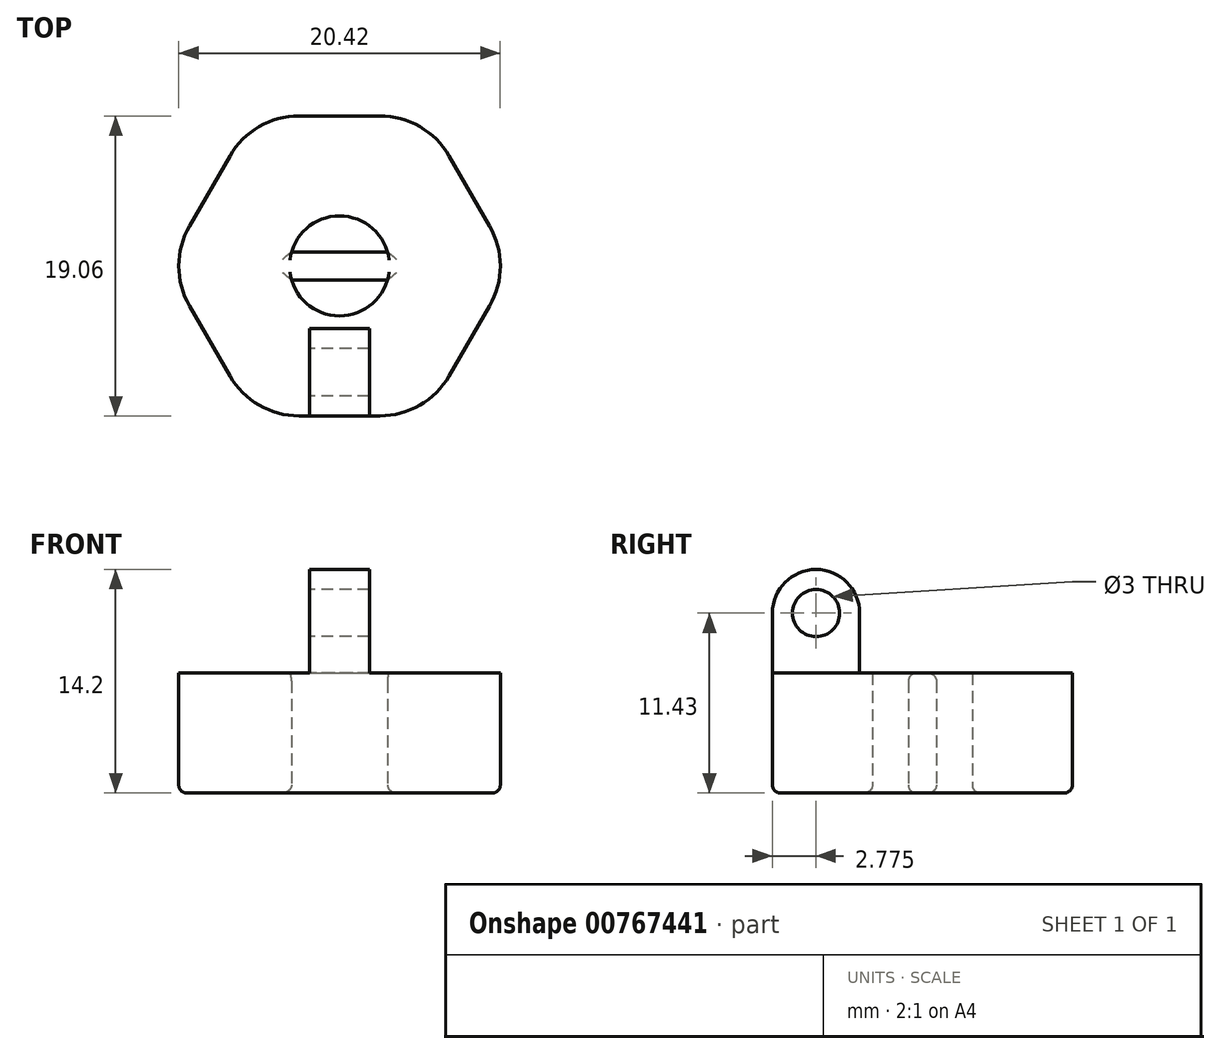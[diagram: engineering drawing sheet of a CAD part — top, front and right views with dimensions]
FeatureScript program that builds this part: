
annotation { "Feature Type Name" : "Feature", "Feature Type Description" : "" }
export const myFeature = defineFeature(function(context is Context, id is Id, definition is map)
    precondition{}
    {
        {
            var Q0;
            Q0=qCreatedBy(makeId("Top.planeOp"),FACE);
            var sketch = newSketch(context, id + "F0", { "sketchPlane" : qUnion([Q0])});
            skCircle(sketch, "E0.cCircle", {"center": v(0, 0) * mm, "radius": 9.53 * mm, "construction": true});
            skLineSegment(sketch, "E0.0", {"start": v(5.5, 9.53) * mm, "end": v(11, 0) * mm});
            skLineSegment(sketch, "E0.1", {"start": v(11, 0) * mm, "end": v(5.5, -9.53) * mm});
            skLineSegment(sketch, "E0.2", {"start": v(5.5, -9.53) * mm, "end": v(-5.5, -9.53) * mm});
            skLineSegment(sketch, "E0.3", {"start": v(-5.5, -9.53) * mm, "end": v(-11, 0) * mm});
            skLineSegment(sketch, "E0.4", {"start": v(-11, 0) * mm, "end": v(-5.5, 9.52) * mm});
            skLineSegment(sketch, "E0.5", {"start": v(-5.5, 9.52) * mm, "end": v(5.5, 9.52) * mm});
            skPoint(sketch, "E0.0.midPoint", {"position": v(8.25, 4.76) * mm});
            skCircle(sketch, "E1", {"center": v(0, 0) * mm, "radius": 3.18 * mm});
            skLineSegment(sketch, "E2.bottom", {"start": v(3.05, -0.89) * mm, "end": v(3.05, 0.89) * mm});
            skLineSegment(sketch, "E2.top", {"start": v(-3.05, -0.89) * mm, "end": v(-3.05, 0.89) * mm});
            skLineSegment(sketch, "E2.left", {"start": v(3.05, -0.89) * mm, "end": v(-3.05, -0.89) * mm});
            skLineSegment(sketch, "E2.right", {"start": v(3.05, 0.89) * mm, "end": v(-3.05, 0.89) * mm});
            skSolve(sketch);
        }
        {
            var Q0;
            Q0 = qSketchRegion(id + "F0", true);
            var Q1;
            Q1=makeQuery(id+"F0.imprint","IMPRINT",FACE,{"disambiguationData":[TD([[makeQuery(id+"F0.imprint","IMPRINT",EDGE,{"derivedFrom":sQuery(id+"F0.wireOp",EDGE,"E2.bottom")}),1.0]])]});
            var Q2;
            {var subQ0=sQuery(id+"F0.wireOp",EDGE,"E2.top");Q2=makeQuery(id+"F0.imprint","IMPRINT",FACE,{"disambiguationData":[TD([[makeQuery(id+"F0.imprint","IMPRINT",EDGE,{"derivedFrom":subQ0}),1.0]])]});}
            var Q3;
            {var subQ0=sQuery(id+"F0.wireOp",EDGE,"E2.bottom");Q3=makeQuery(id+"F0.imprint","IMPRINT",FACE,{"disambiguationData":[TD([[makeQuery(id+"F0.imprint","IMPRINT",EDGE,{"derivedFrom":subQ0}),-1.0]])]});}
            extrude(context, id + "F1", {"entities" : qUnion([Q0, Q1, Q2, Q3]), "depth" : 7.62 * mm, "offsetDistance" : 25.4 * mm});
        }
        {
            var Q0;
            Q0=qCreatedBy(makeId("Right.planeOp"),FACE);
            var sketch = newSketch(context, id + "F2", { "sketchPlane" : qUnion([Q0])});
            skLineSegment(sketch, "E3.0", {"start": v(0, 7.62) * mm, "end": v(-9.53, 7.62) * mm});
            skLineSegment(sketch, "E4.bottom", {"start": v(-9.53, 7.62) * mm, "end": v(-3.98, 7.62) * mm});
            skLineSegment(sketch, "E4.top", {"start": v(-9.53, 11.43) * mm, "end": v(-3.99, 11.43) * mm, "construction": true});
            skLineSegment(sketch, "E4.left", {"start": v(-9.53, 7.62) * mm, "end": v(-9.53, 11.43) * mm});
            skLineSegment(sketch, "E4.right", {"start": v(-3.98, 7.62) * mm, "end": v(-3.99, 11.43) * mm});
            skCircle(sketch, "E5", {"center": v(-6.76, 11.43) * mm, "radius": 1.5 * mm});
            skArc(sketch, "E6", {"start": v(-3.99, 11.43) * mm, "mid": v(-6.76, 14.2) * mm, "end": v(-9.53, 11.43) * mm});
            skSolve(sketch);
        }
        {
            var Q0;
            Q0 = qSketchRegion(id + "F2", true);
            extrude(context, id + "F3", {"entities" : qUnion([Q0]), "operationType" : NewBodyOperationType.ADD, "depth" : 3.8 * mm, "offsetDistance" : 25.4 * mm, "symmetric" : true});
        }
        {
            var Q0;
            Q0=makeQuery(id+"F1.opExtrude","SWEPT_EDGE",EDGE,{"disambiguationData":[OSD([sQuery(id+"F0.wireOp",EDGE,"E0.2"),sQuery(id+"F0.wireOp",EDGE,"E0.3")])]});
            var Q1;
            Q1=makeQuery(id+"F1.opExtrude","SWEPT_EDGE",EDGE,{"disambiguationData":[OSD([sQuery(id+"F0.wireOp",EDGE,"E0.3"),sQuery(id+"F0.wireOp",EDGE,"E0.4")])]});
            var Q2;
            Q2=makeQuery(id+"F1.opExtrude","SWEPT_EDGE",EDGE,{"disambiguationData":[OSD([sQuery(id+"F0.wireOp",EDGE,"E0.4"),sQuery(id+"F0.wireOp",EDGE,"E0.5")])]});
            var Q3;
            Q3=makeQuery(id+"F1.opExtrude","SWEPT_EDGE",EDGE,{"disambiguationData":[OSD([sQuery(id+"F0.wireOp",EDGE,"E0.0"),sQuery(id+"F0.wireOp",EDGE,"E0.5")])]});
            var Q4;
            Q4=makeQuery(id+"F1.opExtrude","SWEPT_EDGE",EDGE,{"disambiguationData":[OSD([sQuery(id+"F0.wireOp",EDGE,"E0.0"),sQuery(id+"F0.wireOp",EDGE,"E0.1")])]});
            var Q5;
            Q5=makeQuery(id+"F1.opExtrude","SWEPT_EDGE",EDGE,{"disambiguationData":[OSD([sQuery(id+"F0.wireOp",EDGE,"E0.1"),sQuery(id+"F0.wireOp",EDGE,"E0.2")])]});
            fillet(context, id + "F4", {"entities" : qUnion([Q0, Q1, Q2, Q3, Q4, Q5]), "radius" : 5.08 * mm, "tangentPropagation" : true, "allowEdgeOverflow" : false});
        }
        {
            var Q0;
            Q0=makeQuery(id+"F1.opExtrude","CAP_EDGE",EDGE,{"disambiguationData":[OSD([sQuery(id+"F0.wireOp",EDGE,"E2.left")])],"isStart":false});
            var Q1;
            Q1=makeQuery(id+"F1.opExtrude","CAP_EDGE",EDGE,{"disambiguationData":[OSD([sQuery(id+"F0.wireOp",EDGE,"E2.right")])],"isStart":false});
            var Q2;
            Q2=makeQuery(id+"F1.opExtrude","CAP_EDGE",EDGE,{"disambiguationData":[OSD([sQuery(id+"F0.wireOp",EDGE,"E2.left")])],"isStart":true});
            var Q3;
            Q3=makeQuery(id+"F1.opExtrude","CAP_EDGE",EDGE,{"disambiguationData":[OSD([sQuery(id+"F0.wireOp",EDGE,"E2.right")])],"isStart":true});
            var Q4;
            {var subQ0=sQuery(id+"F0.wireOp",EDGE,"E2.left");var subQ1=sQuery(id+"F0.wireOp",EDGE,"E1");Q4=makeQuery(id+"F1.opExtrude","CAP_EDGE",EDGE,{"disambiguationData":[OSD([subQ1]),TDD([makeQuery(id+"F0.imprint","IMPRINT",EDGE,{"disambiguationData":[TD([[makeQuery(id+"F0.imprint","INTERSECT",VERTEX,{"derivedFrom":[subQ1,sQuery(id+"F0.wireOp",EDGE,"E2.bottom"),subQ0]}),1.0]])],"derivedFrom":subQ1})])],"isStart":true});}
            var Q5;
            {var subQ0=sQuery(id+"F0.wireOp",EDGE,"E2.right");var subQ1=sQuery(id+"F0.wireOp",EDGE,"E1");Q5=makeQuery(id+"F1.opExtrude","CAP_EDGE",EDGE,{"disambiguationData":[OSD([subQ1]),TDD([makeQuery(id+"F0.imprint","IMPRINT",EDGE,{"disambiguationData":[TD([[makeQuery(id+"F0.imprint","INTERSECT",VERTEX,{"derivedFrom":[subQ1,sQuery(id+"F0.wireOp",EDGE,"E2.bottom"),subQ0]}),-1.0]])],"derivedFrom":subQ1})])],"isStart":true});}
            var Q6;
            Q6=makeQuery(id+"F1.opExtrude","CAP_EDGE",EDGE,{"disambiguationData":[OSD([sQuery(id+"F0.wireOp",EDGE,"E0.4")])],"isStart":true});
            fillet(context, id + "F5", {"entities" : qUnion([Q0, Q1, Q2, Q3, Q4, Q5, Q6]), "radius" : 0.5 * mm, "tangentPropagation" : true, "allowEdgeOverflow" : false});
        }
    });
